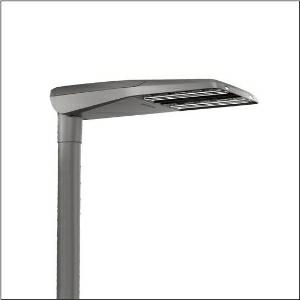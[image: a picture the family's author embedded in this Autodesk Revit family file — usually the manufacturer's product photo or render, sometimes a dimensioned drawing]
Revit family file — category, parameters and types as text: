
# Revit family: streetlight_sl_11_iq_midi___st1_2a_5xc3a11g08me_6871
name_source: partatom
category: Lighting Fixtures
units: mm (PartAtom-declared; Revit-internal decimal feet)

## family parameters
Cut with Voids When Loaded = No
Host = Face
Light Source = No
Part Type = Normal
Room Calculation Point = No
Round Connector Dimension = Use Diameter
Shared = No

## types (1)
- --- (1 x LED, 11170 lm, 124.5 W, 1800K)
    Apparent Load = 125 VA
    CIE Flux Codes = 32 70 96 100 100
    Color Rendering = 70
    Color Temperature = 1800K
    Default Elevation = 1800 mm  [stored 5.90551 ft]
    Description = Streetlight SL 11 iQ midi, mast luminaire, primary light control with 3 zone facetted reflector, of plastic, silver coated, highly specular, primary optical cover: cover, of PMMA, transparent, light distribution: ST1.2a, light emission: direct distribution, primary light characteristic: asymmetric, installation type: post-top, side-entry, lamps: LED, High Power LED, rated values: 11.170lm | 124,5W | 89,7lm/W (begin service life); end service life: 11.170lm | 131,6W; at 50% lumin. flux: 5.585lm | 55,1W | 101,4lm/W, colour temperature: 1800K, colour rendering: CRI > 70, light colour: 718, light setting 1 begin service life: 100% | 11.170lm | 124,5W | 89,7lm/W | 1.800K, light setting 1 end service life: 131,6W, further light settings possible, control: Street-Remote, Auto-Match, Temp-Guard, Lumen-Switch, Night-Set, Smart-Wire, Light-Fading, Desk-Remote (wireless, voltage-free reading and setting of iQ features in the workshop via application-optimized NFC function/RFID function), optimised constant luminous flux control (CLO 2.0), pre-setting: linear dimming characteristic, with cable H07RN-F 5x 1.5mm², mains connection: 230..240V, AC, 50/60Hz, connection cable pre-assembled, cable length: 12,5m, luminaire housing, of diecast aluminium, powder-coated, SITECO metallic grey (DB 702S), please order mast flange separately, inclination adjustable without tools: 0°, 5°, 10°, 15° (post-top) | 0°, -5°, -10°, -15° (side-entry), sealing non-destructively replaceable, multi-level sealing system, length: 780mm, width: 376mm, height: 118mm, mast flange for spigot size: 42mm (side-entry): 5XC10008XM4, 60/48mm (side-entry/post-top): 5XC10108XM2, 76/60mm (side-entry/post-top): 5XC10108XM1, equipment: Power, protection rating (complete): IP66, insulation class (complete): insulation class II (safety insulation), certification: CE, ENEC, ENEC+, VDE, impact resistance: IK10, permissible operating ambient temperature for outdoor applications: -25..+50°C, standard-compliant lighting for roads and squares, Environmental Product Declaration (EPD) tested and certified by an independent institute, packaging unit: 1 piece

Light Distribution: ST1.2a
    Height = 118 mm
    Lamp = 1 x LED
    Lamp Light Flux = 11170 lm
    Lamp Power = 124.5 W
    Lamp count = 1
    Length = 780 mm
    Luminous efficacy = 90 lm/W
    Manufacturer = Siteco
    ModVariant = No
    Model = 5XC3A11G08ME
    Number of Poles = 1
    OnlyDefault = Yes
    Power Factor = 1
    Product Name = Streetlight SL 11 iQ midi | ST1.2a
    Product group = mast luminaire | pylon top
    ProductGroupID = 6100
    Protection Class = Protection class II
    Protection Degree = IP 66
    RLX_Detail_Level = 1
    RLX_Emergency_Light_Flux = 0 lm
    RLX_Emergency_Type = 0
    RLX_Emergency_Type_DB = No
    RlxData = <blob elided: 71097 chars, md5=54670342>
    Socket = socket
    Standby Power = 0 W
    System Light Flux = 11170 lm
    System Power = 125 W
    Type Comments = factory setting: luminous flux: 100 % | dim-lin: 254 | 554 mA
    Type Image = l_1005960.jpg
    URL = http://relux.com
    VarID = @adj_086073
    Voltage = 0 V
    Weight = 0.00 kg
    Width = 376 mm

note: [stored X ft] marks values corroborated as IEEE doubles in the binary element streams (Revit-internal decimal feet)

## geometry (parser evidence)
native form markers: Blend x4, Sweep x11
no freeform markers — native parametric forms only
